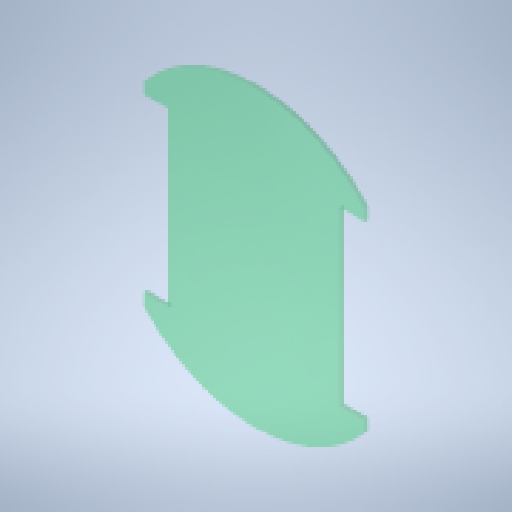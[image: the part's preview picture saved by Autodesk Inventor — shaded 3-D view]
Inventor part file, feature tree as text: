
AUTODESK INVENTOR PART (.ipt)
format: ipt  version: 2025.3 (Build 293356000, 356)  size: 266,240 bytes
history: native  units: mm
features: sketch x3, extrude x2, other x1, hole x1
ambient origin geometry x8: Origin, YZ Plane, XZ Plane, XY Plane, X Axis, Y Axis, Z Axis, Center Point
bodies: Body1 (feature_tree)
feature tree (7):
  other  "ソリッド1"
  extrude  "基板"  Depth=130.0mm
  hole  "ギヤボックス取付穴"  [1 undecoded]
  extrude  "エンコーダ取出し穴"  Depth=1.6mm TaperAngle=0.0deg
  sketch  "スケッチ1"
  sketch  "スケッチ2"
  sketch  "スケッチ3"
note: 1 required parameter value undecoded (feature->parameter linkage not recoverable at this tier; creation-order binding heuristic only, values carry confidence <= 0.55)
